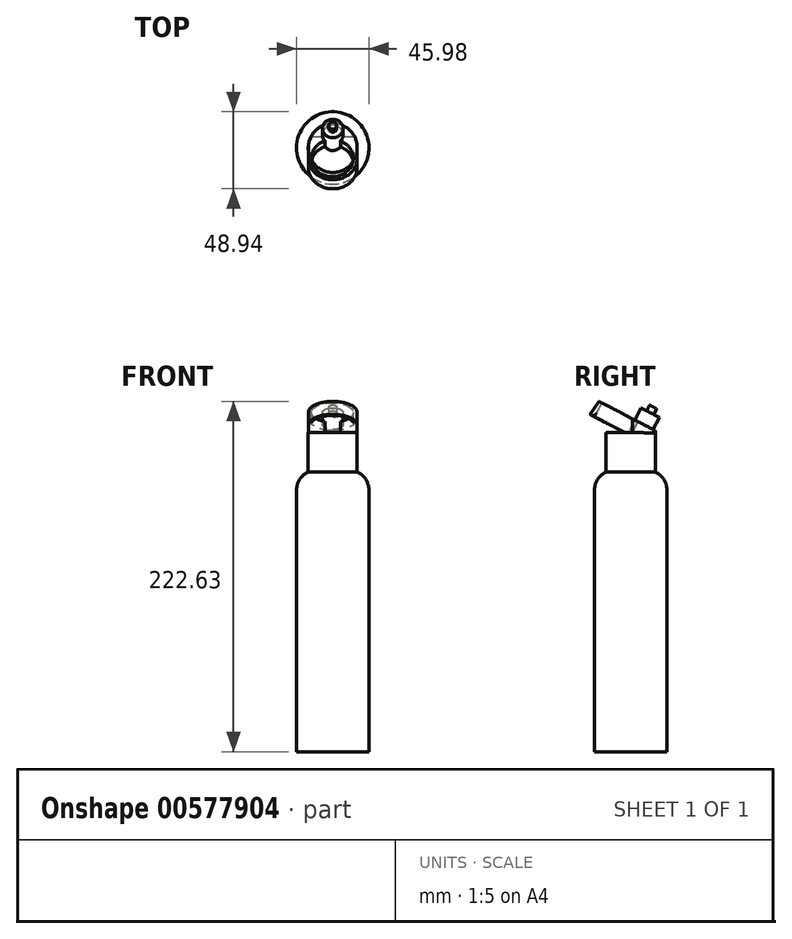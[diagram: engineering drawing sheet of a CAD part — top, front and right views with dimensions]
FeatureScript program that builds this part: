
annotation { "Feature Type Name" : "Feature", "Feature Type Description" : "" }
export const myFeature = defineFeature(function(context is Context, id is Id, definition is map)
    precondition{}
    {
        {
            var Q0;
            Q0=qCreatedBy(makeId("Top.planeOp"),FACE);
            var sketch = newSketch(context, id + "F0", { "sketchPlane" : qUnion([Q0])});
            skCircle(sketch, "E0", {"center": v(0, 0) * mm, "radius": 22.99 * mm});
            skSolve(sketch);
        }
        {
            var Q0;
            Q0 = qSketchRegion(id + "F0", true);
            extrude(context, id + "F1", {"entities" : qUnion([Q0]), "depth" : 177.8 * mm, "offsetDistance" : 25.4 * mm});
        }
        {
            var Q0;
            Q0=makeQuery(id+"F1.opExtrude","CAP_FACE",FACE,{"disambiguationData":[OSD([sQuery(id+"F0.wireOp",EDGE,"E0")])],"isStart":false});
            var sketch = newSketch(context, id + "F2", { "sketchPlane" : qUnion([Q0])});
            skCircle(sketch, "E1", {"center": v(0, 0) * mm, "radius": 15.56 * mm});
            skSolve(sketch);
        }
        {
            var Q0;
            Q0 = qSketchRegion(id + "F2", true);
            extrude(context, id + "F3", {"entities" : qUnion([Q0]), "operationType" : NewBodyOperationType.ADD, "depth" : 24.9 * mm, "offsetDistance" : 25.4 * mm});
        }
        {
            var Q0;
            Q0=makeQuery(id+"F1.opExtrude","CAP_EDGE",EDGE,{"disambiguationData":[OSD([sQuery(id+"F0.wireOp",EDGE,"E0")])],"isStart":false});
            fillet(context, id + "F4", {"entities" : qUnion([Q0]), "radius" : 12.7 * mm, "tangentPropagation" : true, "allowEdgeOverflow" : false});
        }
        {
            var Q0;
            Q0=makeQuery(id+"F3.opExtrude","CAP_EDGE",EDGE,{"disambiguationData":[OSD([sQuery(id+"F2.wireOp",EDGE,"E1")])],"isStart":false});
            cPlane(context, id + "F5", {"entities" : qUnion([Q0]), "cplaneType" : CPlaneType.LINE_ANGLE, "offset" : 25.4 * mm, "angle" : 0 * degree, "width" : 152.4 * mm, "height" : 152.4 * mm});
        }
        {
            var Q0;
            Q0=qCreatedBy(id+"F5.planeOp",FACE);
            var sketch = newSketch(context, id + "F6", { "sketchPlane" : qUnion([Q0])});
            skLineSegment(sketch, "E2", {"start": v(-3.7, 202.8) * mm, "end": v(-25.95, 214.36) * mm});
            skLineSegment(sketch, "E3", {"start": v(-25.95, 214.36) * mm, "end": v(-20.17, 222.63) * mm});
            skLineSegment(sketch, "E4", {"start": v(-20.17, 222.63) * mm, "end": v(15.56, 204.05) * mm});
            skLineSegment(sketch, "E5", {"start": v(15.56, 204.05) * mm, "end": v(15.56, 202.6) * mm});
            skLineSegment(sketch, "E6", {"start": v(-3.7, 202.8) * mm, "end": v(15.56, 202.6) * mm});
            skSolve(sketch);
        }
        {
            var Q0;
            Q0=makeQuery(id+"F6.imprint","IMPRINT",FACE,{"disambiguationData":[TD([[makeQuery(id+"F6.imprint","IMPRINT",EDGE,{"derivedFrom":sQuery(id+"F6.wireOp",EDGE,"E2")}),-1.0]])]});
            extrude(context, id + "F7", {"entities" : qUnion([Q0]), "operationType" : NewBodyOperationType.ADD, "depth" : 15.54 * mm, "offsetDistance" : 25.4 * mm, "hasSecondDirection" : true, "secondDirectionOppositeDirection" : true, "secondDirectionDepth" : 15.5 * mm});
        }
        {
            var Q0;
            Q0=makeQuery(id+"F7.opExtrude","SWEPT_FACE",FACE,{"disambiguationData":[OSD([sQuery(id+"F6.wireOp",EDGE,"E6")])]});
            var sketch = newSketch(context, id + "F8", { "sketchPlane" : qUnion([Q0])});
            skArc(sketch, "E7", {"start": v(-15.5, 2) * mm, "mid": v(-10.95, -9) * mm, "end": v(0.03, -13.57) * mm});
            skPoint(sketch, "E7.startSnap0", {"position": v(-15.56, 2) * mm});
            skLineSegment(sketch, "E8", {"start": v(0.03, -13.57) * mm, "end": v(0.03, -27) * mm});
            skLineSegment(sketch, "E9", {"start": v(0.03, -27) * mm, "end": v(-31.15, -11.06) * mm});
            skLineSegment(sketch, "E10", {"start": v(-31.15, -11.06) * mm, "end": v(-15.5, 2) * mm});
            skSolve(sketch);
        }
        {
            var Q0;
            Q0 = qSketchRegion(id + "F8", true);
            extrude(context, id + "F9", {"entities" : qUnion([Q0]), "operationType" : NewBodyOperationType.REMOVE, "oppositeDirection" : true, "depth" : 25.4 * mm, "offsetDistance" : 25.4 * mm});
        }
        {
            var Q0;
            Q0=makeQuery(id+"F7.opExtrude","SWEPT_FACE",FACE,{"disambiguationData":[OSD([sQuery(id+"F6.wireOp",EDGE,"E6")])]});
            var sketch = newSketch(context, id + "F10", { "sketchPlane" : qUnion([Q0])});
            skArc(sketch, "E11", {"start": v(0.03, -13.57) * mm, "mid": v(10.65, -9.42) * mm, "end": v(15.54, 0.88) * mm});
            skLineSegment(sketch, "E12", {"start": v(15.54, 0.88) * mm, "end": v(26, -13.56) * mm});
            skLineSegment(sketch, "E13", {"start": v(26, -13.56) * mm, "end": v(7.37, -18.34) * mm});
            skLineSegment(sketch, "E14", {"start": v(7.37, -18.34) * mm, "end": v(0.03, -13.57) * mm});
            skSolve(sketch);
        }
        {
            var Q0;
            Q0 = qSketchRegion(id + "F10", true);
            extrude(context, id + "F11", {"entities" : qUnion([Q0]), "operationType" : NewBodyOperationType.REMOVE, "oppositeDirection" : true, "depth" : 25.4 * mm, "offsetDistance" : 25.4 * mm});
        }
        {
            var Q0;
            Q0=makeQuery(id+"F7.opExtrude","CAP_EDGE",EDGE,{"disambiguationData":[OSD([sQuery(id+"F6.wireOp",EDGE,"E3")])],"isStart":true});
            var Q1;
            Q1=makeQuery(id+"F7.opExtrude","CAP_EDGE",EDGE,{"disambiguationData":[OSD([sQuery(id+"F6.wireOp",EDGE,"E3")])],"isStart":false});
            fillet(context, id + "F12", {"entities" : qUnion([Q0, Q1]), "radius" : 15.24 * mm, "tangentPropagation" : true, "allowEdgeOverflow" : false});
        }
        {
            var Q0;
            Q0=makeQuery(id+"F7.opExtrude","SWEPT_FACE",FACE,{"disambiguationData":[OSD([sQuery(id+"F6.wireOp",EDGE,"E4")])]});
            var sketch = newSketch(context, id + "F13", { "sketchPlane" : qUnion([Q0])});
            skCircle(sketch, "E15", {"center": v(-0.25, -105.2) * mm, "radius": 13.31 * mm});
            skSolve(sketch);
        }
        {
            var Q0;
            Q0 = qSketchRegion(id + "F13", true);
            var Q1;
            Q1=makeQuery(id+"F3.opExtrude","CAP_FACE",FACE,{"disambiguationData":[OSD([sQuery(id+"F2.wireOp",EDGE,"E1")])],"isStart":false});
            extrude(context, id + "F14", {"entities" : qUnion([Q0]), "operationType" : NewBodyOperationType.REMOVE, "endBound" : BoundingType.UP_TO_SURFACE, "oppositeDirection" : true, "depth" : 10.16 * mm, "endBoundEntityFace" : qUnion([Q1]), "offsetDistance" : 25.4 * mm});
        }
        {
            var Q0;
            Q0=makeQuery(id+"F7.opExtrude","SWEPT_FACE",FACE,{"disambiguationData":[OSD([sQuery(id+"F6.wireOp",EDGE,"E4")])]});
            var sketch = newSketch(context, id + "F15", { "sketchPlane" : qUnion([Q0])});
            skCircle(sketch, "E16", {"center": v(0, -88.4) * mm, "radius": 6.59 * mm});
            skSolve(sketch);
        }
        {
            var Q0;
            Q0 = qSketchRegion(id + "F15", true);
            extrude(context, id + "F16", {"entities" : qUnion([Q0]), "operationType" : NewBodyOperationType.ADD, "depth" : 8.64 * mm, "offsetDistance" : 25.4 * mm, "hasSecondDirection" : true, "secondDirectionOppositeDirection" : true, "secondDirectionDepth" : 25.4 * mm});
        }
        {
            var Q0;
            Q0=makeQuery(id+"F14.boolean.opBoolean","COPY",EDGE,{"derivedFrom":makeQuery(id+"F14.opExtrude","CAP_EDGE",EDGE,{"disambiguationData":[OSD([sQuery(id+"F13.wireOp",EDGE,"E15")])],"isStart":true})});
            var Q1;
            Q1=makeQuery(id+"F14.boolean.opBoolean","INTERSECT",EDGE,{"derivedFrom":[makeQuery(id+"F7.opExtrude","SWEPT_FACE",FACE,{"disambiguationData":[OSD([sQuery(id+"F6.wireOp",EDGE,"E2")])]}),makeQuery(id+"F14.opExtrude","SWEPT_FACE",FACE,{"disambiguationData":[OSD([sQuery(id+"F13.wireOp",EDGE,"E15")])]})]});
            fillet(context, id + "F17", {"entities" : qUnion([Q0, Q1]), "radius" : 2.54 * mm, "tangentPropagation" : true, "allowEdgeOverflow" : false});
        }
        {
            var Q0;
            Q0=makeQuery(id+"F16.opExtrude","CAP_FACE",FACE,{"disambiguationData":[OSD([sQuery(id+"F15.wireOp",EDGE,"E16")])],"isStart":false});
            var sketch = newSketch(context, id + "F18", { "sketchPlane" : qUnion([Q0])});
            skCircle(sketch, "E17", {"center": v(0, -88.4) * mm, "radius": 2.54 * mm});
            skSolve(sketch);
        }
        {
            var Q0;
            Q0 = qSketchRegion(id + "F18", true);
            extrude(context, id + "F19", {"entities" : qUnion([Q0]), "operationType" : NewBodyOperationType.ADD, "depth" : 4.06 * mm, "offsetDistance" : 25.4 * mm});
        }
    });
